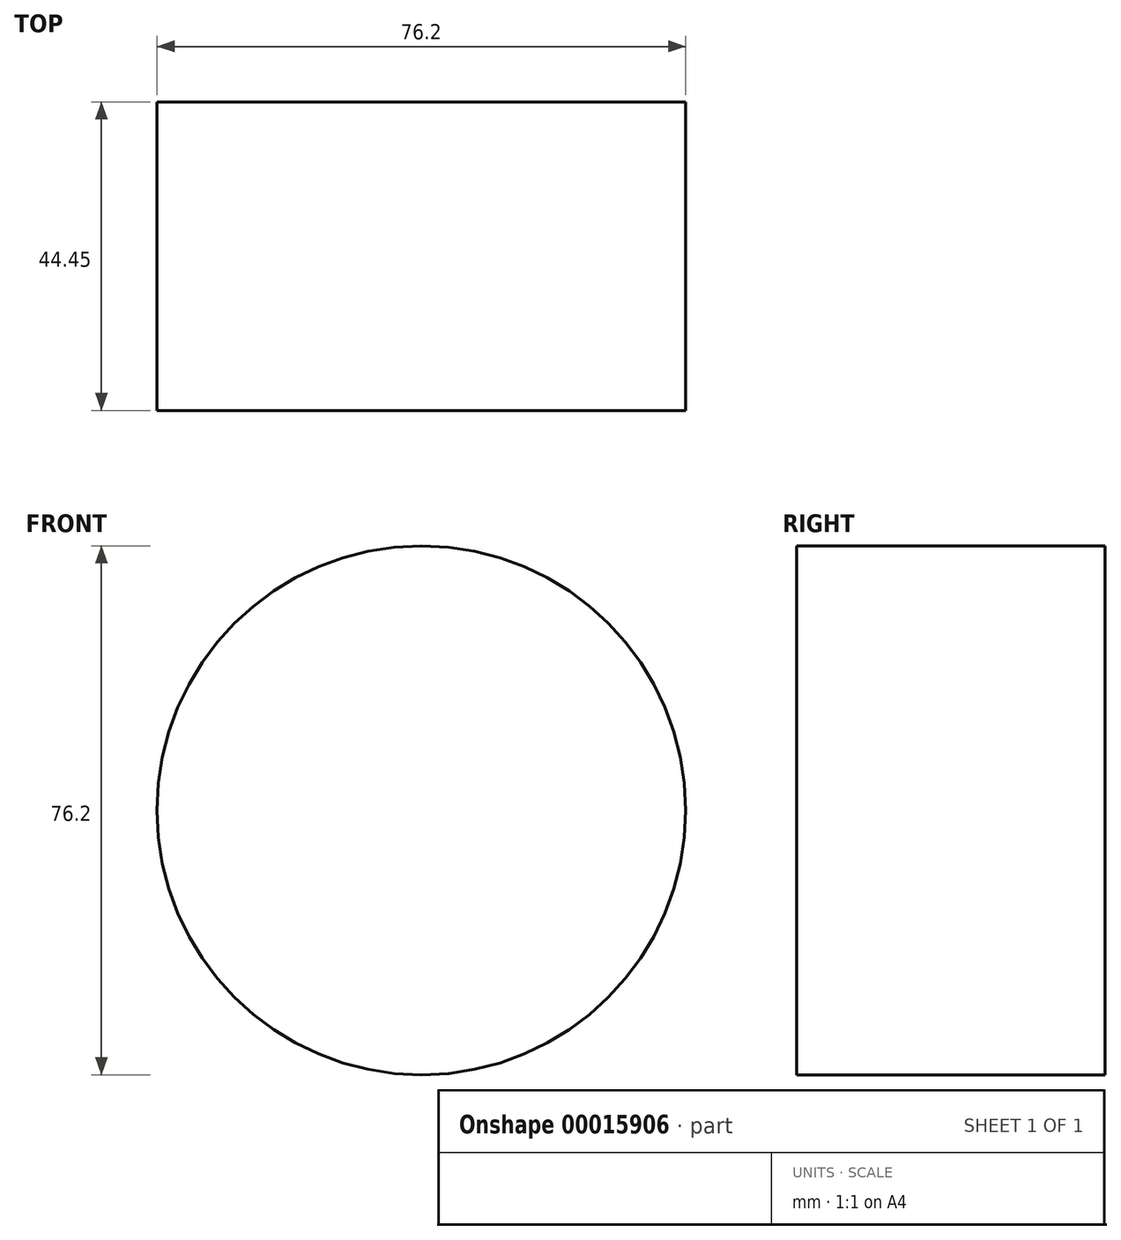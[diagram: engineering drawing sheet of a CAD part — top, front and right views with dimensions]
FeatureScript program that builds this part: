
annotation { "Feature Type Name" : "Feature", "Feature Type Description" : "" }
export const myFeature = defineFeature(function(context is Context, id is Id, definition is map)
    precondition{}
    {
        {
            var Q0;
            Q0=qCreatedBy(makeId("Front.planeOp"),FACE);
            var sketch = newSketch(context, id + "F0", { "sketchPlane" : qUnion([Q0])});
            skCircle(sketch, "E0", {"center": v(0, 0) * mm, "radius": 38.1 * mm});
            skSolve(sketch);
        }
        {
            var Q0;
            Q0=makeQuery(id+"F0.imprint","IMPRINT",FACE,{"disambiguationData":[TD([[makeQuery(id+"F0.imprint","IMPRINT",EDGE,{"derivedFrom":sQuery(id+"F0.wireOp",EDGE,"E0")}),1.0]])]});
            extrude(context, id + "F1", {"entities" : qUnion([Q0]), "depth" : 44.45 * mm});
        }
    });
